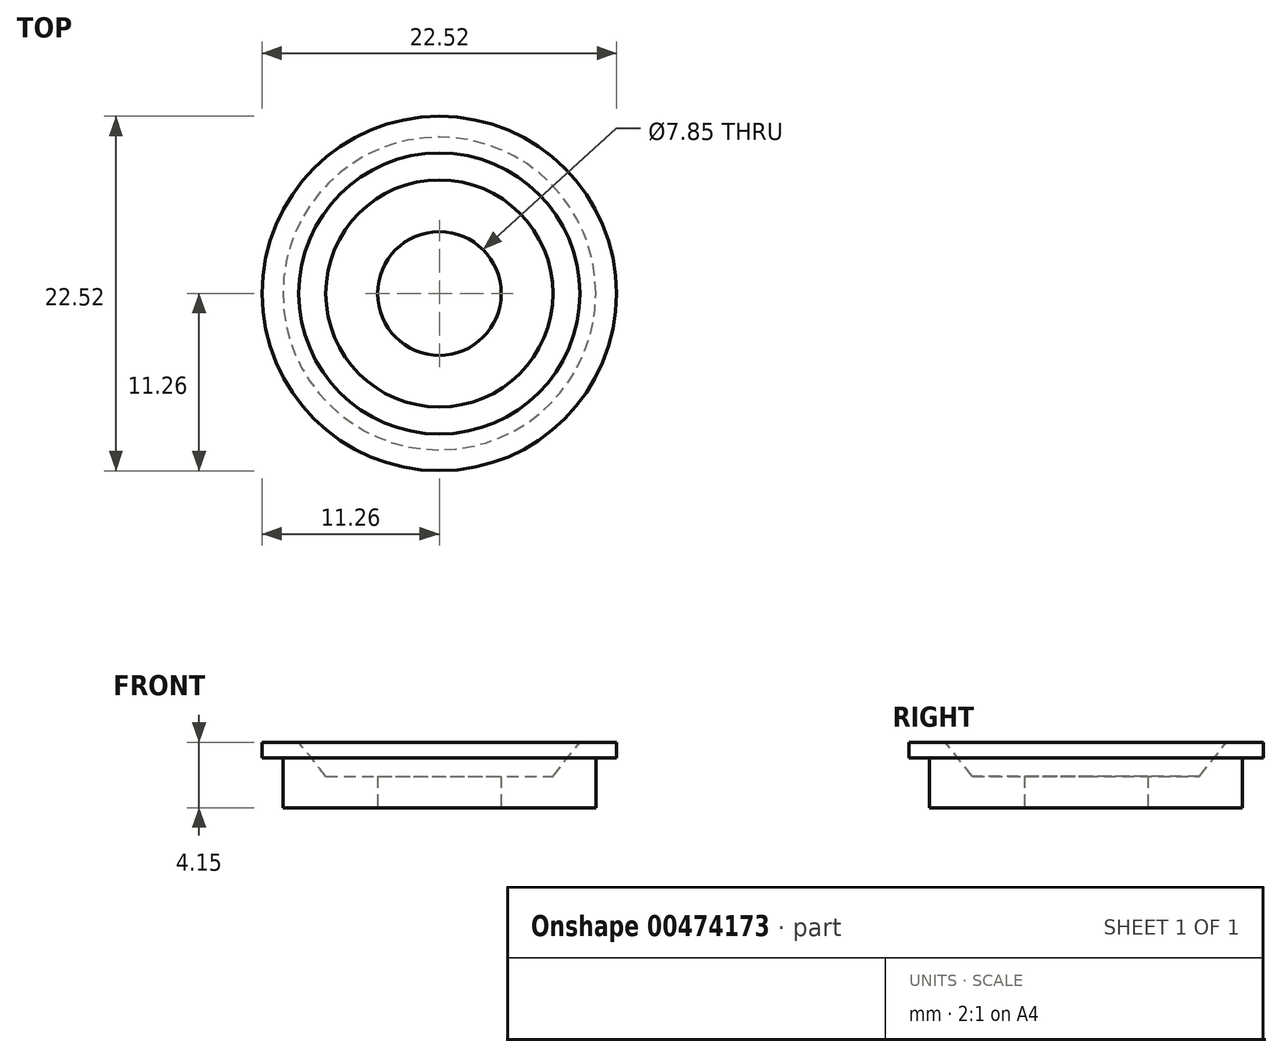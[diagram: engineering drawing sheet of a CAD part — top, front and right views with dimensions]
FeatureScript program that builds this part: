
annotation { "Feature Type Name" : "Feature", "Feature Type Description" : "" }
export const myFeature = defineFeature(function(context is Context, id is Id, definition is map)
    precondition{}
    {
        {
            var Q0;
            Q0=qCreatedBy(makeId("Right.planeOp"),FACE);
            var sketch = newSketch(context, id + "F0", { "sketchPlane" : qUnion([Q0])});
            skLineSegment(sketch, "E0", {"start": v(0, 0) * mm, "end": v(0, 0.01) * mm});
            skLineSegment(sketch, "E1", {"start": v(3.92, 0) * mm, "end": v(3.92, 2) * mm});
            skLineSegment(sketch, "E2", {"start": v(3.92, 2) * mm, "end": v(7.21, 2) * mm});
            skLineSegment(sketch, "E3", {"start": v(7.21, 2) * mm, "end": v(8.92, 4.15) * mm});
            skLineSegment(sketch, "E4", {"start": v(8.93, 4.15) * mm, "end": v(11.26, 4.15) * mm});
            skLineSegment(sketch, "E5", {"start": v(11.26, 4.15) * mm, "end": v(11.26, 3.15) * mm});
            skLineSegment(sketch, "E6", {"start": v(11.26, 3.15) * mm, "end": v(9.94, 3.15) * mm});
            skLineSegment(sketch, "E7", {"start": v(9.94, 3.15) * mm, "end": v(9.94, 0) * mm});
            skLineSegment(sketch, "E8", {"start": v(9.94, 0) * mm, "end": v(3.92, 0) * mm});
            skSolve(sketch);
        }
        {
            var Q0;
            Q0 = qSketchRegion(id + "F0", true);
            var Q1;
            Q1=sQuery(id+"F0.wireOp",EDGE,"E0");
            revolve(context, id + "F1", {"entities" : qUnion([Q0]), "axis" : qUnion([Q1]), "revolveType" : RevolveType.FULL});
        }
    });
